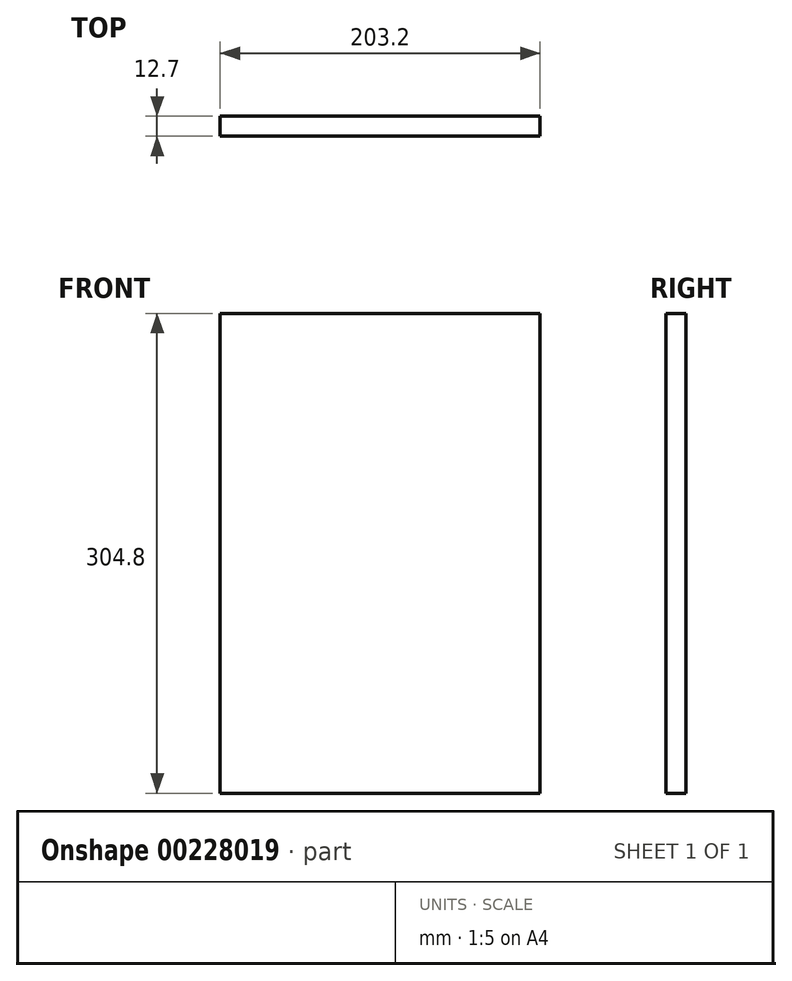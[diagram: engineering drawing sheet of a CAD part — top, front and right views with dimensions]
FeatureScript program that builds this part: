
annotation { "Feature Type Name" : "Feature", "Feature Type Description" : "" }
export const myFeature = defineFeature(function(context is Context, id is Id, definition is map)
    precondition{}
    {
        {
            var Q0;
            Q0=qCreatedBy(makeId("Front.planeOp"),FACE);
            var sketch = newSketch(context, id + "F0", { "sketchPlane" : qUnion([Q0])});
            skLineSegment(sketch, "E0.bottom", {"start": v(101.6, 152.4) * mm, "end": v(-101.6, 152.4) * mm});
            skLineSegment(sketch, "E0.top", {"start": v(101.6, -152.4) * mm, "end": v(-101.6, -152.4) * mm});
            skLineSegment(sketch, "E0.left", {"start": v(101.6, 152.4) * mm, "end": v(101.6, -152.4) * mm});
            skLineSegment(sketch, "E0.right", {"start": v(-101.6, 152.4) * mm, "end": v(-101.6, -152.4) * mm});
            skPoint(sketch, "E0.middle", {"position": v(0, 0) * mm});
            skSolve(sketch);
        }
        {
            var Q0;
            Q0=makeQuery(id+"F0.imprint","IMPRINT",FACE,{"disambiguationData":[TD([[makeQuery(id+"F0.imprint","IMPRINT",EDGE,{"derivedFrom":sQuery(id+"F0.wireOp",EDGE,"E0.bottom")}),1.0]])]});
            extrude(context, id + "F1", {"entities" : qUnion([Q0]), "depth" : 12.7 * mm});
        }
    });
